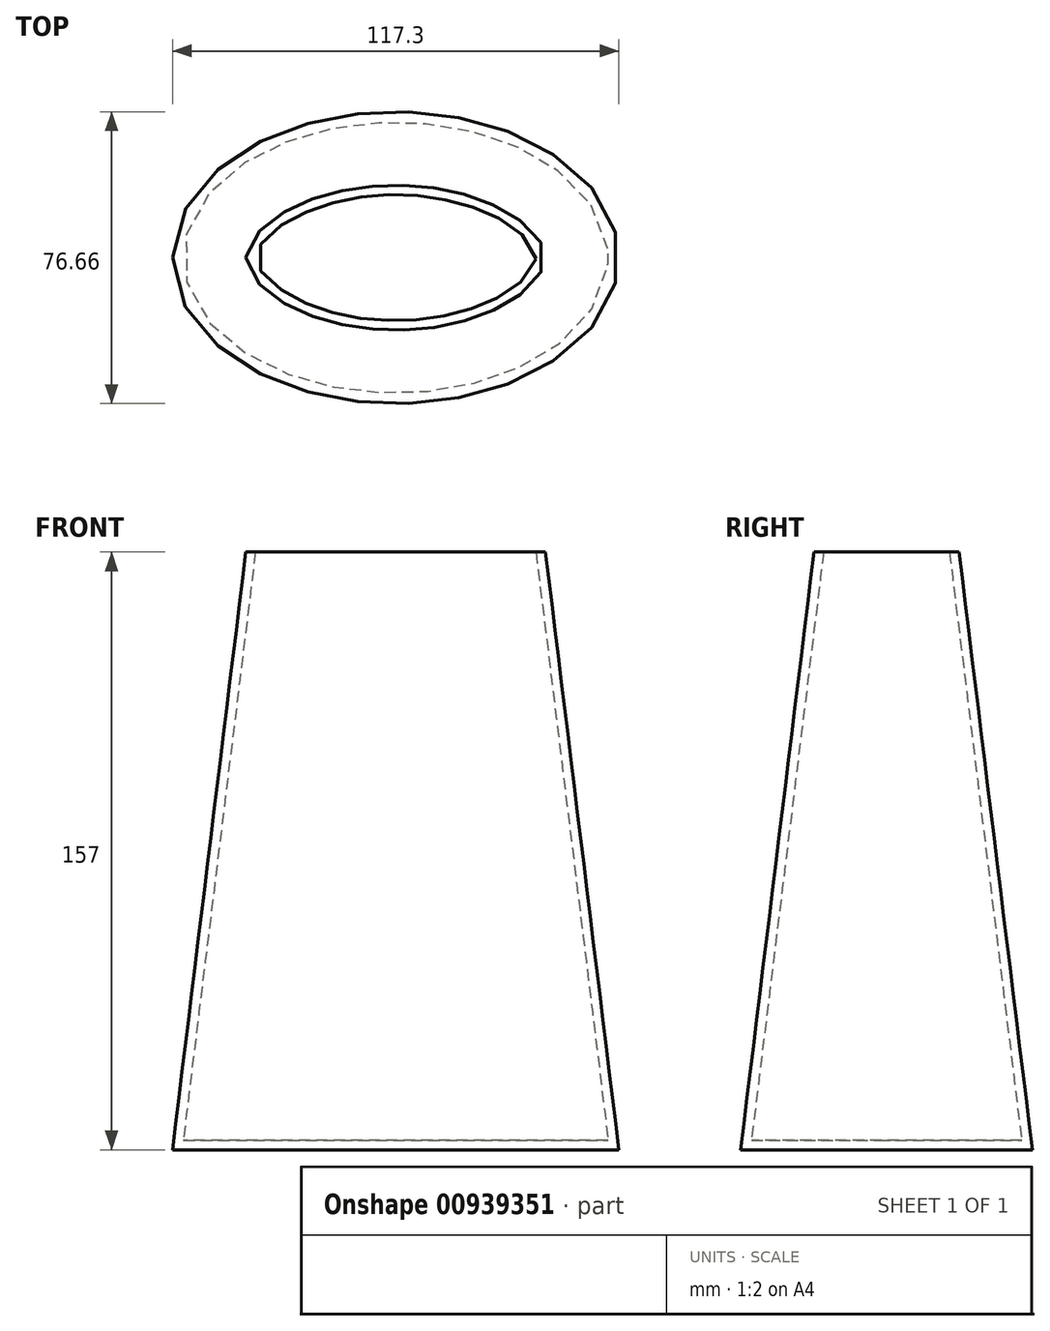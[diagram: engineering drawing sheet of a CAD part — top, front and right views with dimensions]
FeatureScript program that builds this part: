
annotation { "Feature Type Name" : "Feature", "Feature Type Description" : "" }
export const myFeature = defineFeature(function(context is Context, id is Id, definition is map)
    precondition{}
    {
        {
            var Q0;
            Q0=qCreatedBy(makeId("Top.planeOp"),FACE);
            var sketch = newSketch(context, id + "F0", { "sketchPlane" : qUnion([Q0])});
            skEllipse(sketch, "E0", {"center": v(0, 0) * mm, "majorRadius": 58.65 * mm, "minorRadius": 38.33 * mm, "majorAxis": v(1, 0)});
            skSolve(sketch);
        }
        {
            var Q0;
            Q0=makeQuery(id+"F0.imprint","IMPRINT",FACE,{"disambiguationData":[TD([[makeQuery(id+"F0.imprint","IMPRINT",EDGE,{"derivedFrom":sQuery(id+"F0.wireOp",EDGE,"E0")}),1.0]])]});
            extrude(context, id + "F1", {"entities" : qUnion([Q0]), "depth" : 157 * mm, "offsetDistance" : 25 * mm, "hasDraft" : true, "draftAngle" : 7 * degree, "draftPullDirection" : true});
        }
        {
            var Q0;
            Q0=makeQuery(id+"F1.opExtrude","CAP_FACE",FACE,{"disambiguationData":[OSD([sQuery(id+"F0.wireOp",EDGE,"E0")])],"isStart":false});
            shell(context, id + "F2", {"entities" : qUnion([Q0]), "thickness" : 2.5 * mm});
        }
    });
